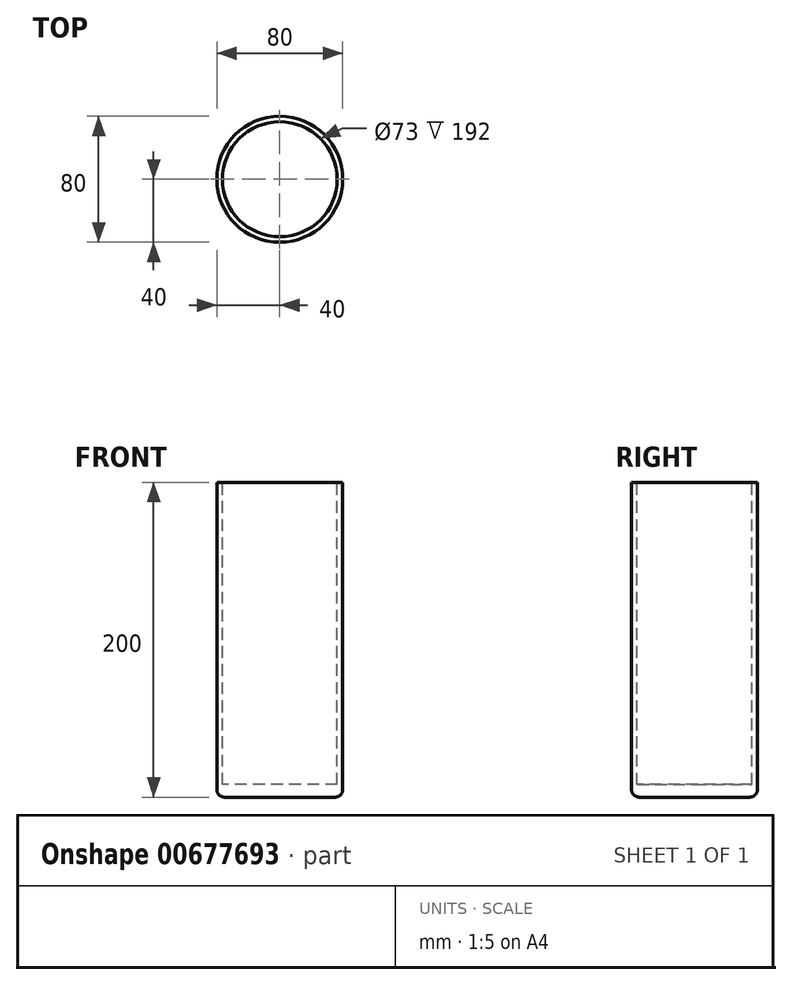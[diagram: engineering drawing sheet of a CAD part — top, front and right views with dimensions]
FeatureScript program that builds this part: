
annotation { "Feature Type Name" : "Feature", "Feature Type Description" : "" }
export const myFeature = defineFeature(function(context is Context, id is Id, definition is map)
    precondition{}
    {
        {
            var Q0;
            Q0=qCreatedBy(makeId("Top.planeOp"),FACE);
            var sketch = newSketch(context, id + "F0", { "sketchPlane" : qUnion([Q0])});
            skCircle(sketch, "E0", {"center": v(0, 0) * mm, "radius": 40 * mm});
            skSolve(sketch);
        }
        {
            var Q0;
            Q0=makeQuery(id+"F0.imprint","IMPRINT",FACE,{"disambiguationData":[TD([[makeQuery(id+"F0.imprint","IMPRINT",EDGE,{"derivedFrom":sQuery(id+"F0.wireOp",EDGE,"E0")}),1.0]])]});
            extrude(context, id + "F1", {"entities" : qUnion([Q0]), "depth" : 200 * mm, "offsetDistance" : 25 * mm});
        }
        {
            var Q0;
            Q0=makeQuery(id+"F1.opExtrude","CAP_EDGE",EDGE,{"disambiguationData":[OSD([sQuery(id+"F0.wireOp",EDGE,"E0")])],"isStart":true});
            fillet(context, id + "F2", {"entities" : qUnion([Q0]), "radius" : 5 * mm, "tangentPropagation" : true, "allowEdgeOverflow" : false});
        }
        {
            var Q0;
            Q0=makeQuery(id+"F1.opExtrude","CAP_FACE",FACE,{"disambiguationData":[OSD([sQuery(id+"F0.wireOp",EDGE,"E0")])],"isStart":false});
            var sketch = newSketch(context, id + "F3", { "sketchPlane" : qUnion([Q0])});
            skCircle(sketch, "E1", {"center": v(0, 0) * mm, "radius": 36.5 * mm});
            skSolve(sketch);
        }
        {
            var Q0;
            Q0=makeQuery(id+"F3.imprint","IMPRINT",FACE,{"disambiguationData":[TD([[makeQuery(id+"F3.imprint","IMPRINT",EDGE,{"derivedFrom":sQuery(id+"F3.wireOp",EDGE,"E1")}),1.0]])]});
            extrude(context, id + "F4", {"entities" : qUnion([Q0]), "operationType" : NewBodyOperationType.REMOVE, "oppositeDirection" : true, "depth" : 192 * mm, "offsetDistance" : 25 * mm});
        }
    });
